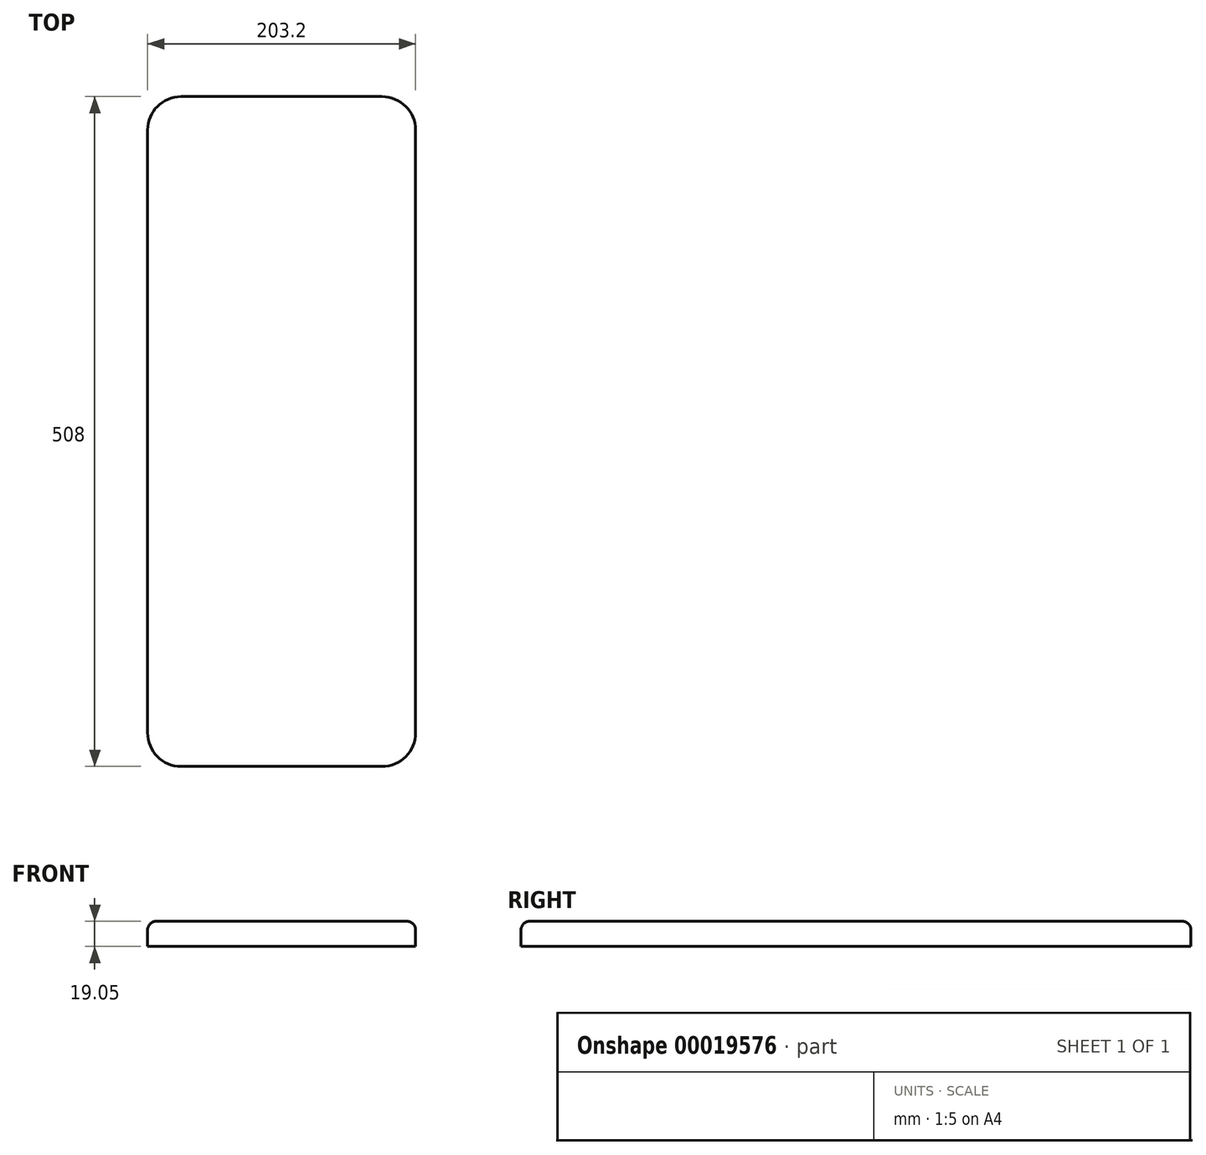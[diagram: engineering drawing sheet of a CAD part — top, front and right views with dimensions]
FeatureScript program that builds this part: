
annotation { "Feature Type Name" : "Feature", "Feature Type Description" : "" }
export const myFeature = defineFeature(function(context is Context, id is Id, definition is map)
    precondition{}
    {
        {
            var Q0;
            Q0=qCreatedBy(makeId("Front.planeOp"),FACE);
            var sketch = newSketch(context, id + "F0", { "sketchPlane" : qUnion([Q0])});
            skLineSegment(sketch, "E0.bottom", {"start": v(0, 0) * mm, "end": v(203.2, 0) * mm});
            skLineSegment(sketch, "E0.top", {"start": v(0, 19.05) * mm, "end": v(203.2, 19.05) * mm});
            skLineSegment(sketch, "E0.left", {"start": v(0, 0) * mm, "end": v(0, 19.05) * mm});
            skLineSegment(sketch, "E0.right", {"start": v(203.2, 0) * mm, "end": v(203.2, 19.05) * mm});
            skSolve(sketch);
        }
        {
            var Q0;
            Q0=makeQuery(id+"F0.imprint","IMPRINT",FACE,{"disambiguationData":[TD([[makeQuery(id+"F0.imprint","IMPRINT",EDGE,{"derivedFrom":sQuery(id+"F0.wireOp",EDGE,"E0.bottom")}),1.0]])]});
            extrude(context, id + "F1", {"entities" : qUnion([Q0]), "depth" : 508 * mm});
        }
        {
            var Q0;
            Q0=makeQuery(id+"F1.opExtrude","CAP_EDGE",EDGE,{"disambiguationData":[OSD([sQuery(id+"F0.wireOp",EDGE,"E0.right")])],"isStart":false});
            var Q1;
            Q1=makeQuery(id+"F1.opExtrude","CAP_EDGE",EDGE,{"disambiguationData":[OSD([sQuery(id+"F0.wireOp",EDGE,"E0.left")])],"isStart":false});
            var Q2;
            Q2=makeQuery(id+"F1.opExtrude","CAP_EDGE",EDGE,{"disambiguationData":[OSD([sQuery(id+"F0.wireOp",EDGE,"E0.right")])],"isStart":true});
            var Q3;
            Q3=makeQuery(id+"F1.opExtrude","CAP_EDGE",EDGE,{"disambiguationData":[OSD([sQuery(id+"F0.wireOp",EDGE,"E0.left")])],"isStart":true});
            fillet(context, id + "F2", {"entities" : qUnion([Q0, Q1, Q2, Q3]), "radius" : 25.4 * mm, "tangentPropagation" : true, "allowEdgeOverflow" : false});
        }
        {
            var Q0;
            Q0=makeQuery(id+"F1.opExtrude","SWEPT_FACE",FACE,{"disambiguationData":[OSD([sQuery(id+"F0.wireOp",EDGE,"E0.top")])]});
            fillet(context, id + "F3", {"entities" : qUnion([Q0]), "radius" : 6.35 * mm, "tangentPropagation" : true, "allowEdgeOverflow" : false});
        }
    });
